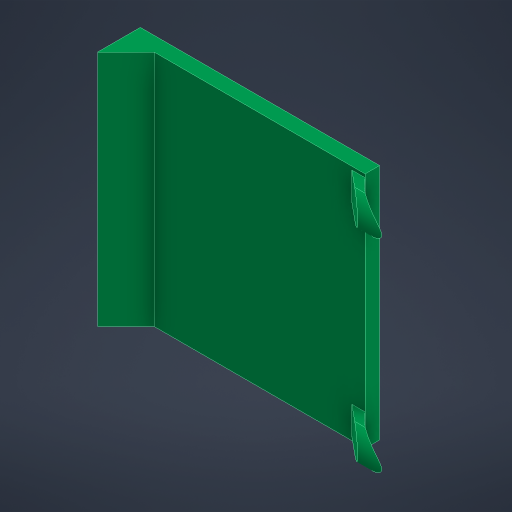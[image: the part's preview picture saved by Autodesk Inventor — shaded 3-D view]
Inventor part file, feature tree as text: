
AUTODESK INVENTOR PART (.ipt)
format: ipt  version: 2023.4 (Build 274418000, 418)  size: 428,032 bytes
history: native  units: mm
features: projected_geometry x15, extrude x8, reference x7, other x4, sketch x2, plane x2, fillet x1, mirror x1, chamfer x1
ambient origin geometry x8: Origin, YZ Plane, XZ Plane, XY Plane, X Axis, Y Axis, Z Axis, Center Point
bodies: Solid1 (feature_tree)
feature tree (41):
  extrude  "Extrusion1"  Depth=4.0mm
  sketch  "Sketch2"  dims[d2=4.0mm d3=4.0mm d4=4.0mm d5=2.0mm d6=2.0mm d7=2.0mm d8=2.0mm d9=3.0mm d10=1.9mm d11=45.0deg d12=33.75mm d13=0.0mm d17=1.5mm d18=0.15mm d19=4.0mm d20=0.0mm d21=2.0mm d22=1.0mm d23=2.5mm d24=0.075mm d28=45.0deg d31=5.0mm d32=0.0mm d37=180.0deg d38=90.0deg d39=67.5deg d40=50.0mm d41=0.0mm d42=18.4mm d43=7.5mm d44=30.0mm d45=10.0mm d46=0.0mm d49=33.75mm d50=0.0mm d52=40.0mm d53=0.0mm d54=0.025mm d55=0.15mm d56=0.15mm d57=10.0mm d58=0.0mm d59=1.35mm d60=2.0mm d61=45.0deg]
  plane  "Work Plane2"
  extrude  "Extrusion2"  Depth=10.0mm
  fillet  "Fillet1"  Radius=4.0mm
  extrude  "Extrusion3"  Depth=10.0mm
  mirror  "Mirror1"
  extrude  "Extrusion5"  Depth=10.0mm
  extrude  "Extrusion6"  Depth=10.0mm
  extrude  "Extrusion7"  Depth=10.0mm
  extrude  "Extrusion8"  Depth=10.0mm
  extrude  "Extrusion9"  Depth=10.0mm
  chamfer  "Chamfer2"  Angle=45.0deg  [1 undecoded]
  sketch  "Sketch1"  dims[d0=0.15mm d1=4.0mm]
  reference  "Reference1"
  reference  "Reference2"
  reference  "Reference3"
  projected_geometry  "Projected Loop1"
  reference  "Reference4"
  reference  "Reference5"
  reference  "Reference6"
  reference  "Reference7"
  other  "Work Point1"
  plane  "Work Plane1"
  projected_geometry  "Projected Loop4"
  projected_geometry  "Projected Loop5"
  projected_geometry  "Projected Loop6"
  projected_geometry  "Projected Loop7"
  projected_geometry  "Projected Loop8"
  projected_geometry  "Projected Loop9"
  projected_geometry  "Projected Loop14"
  projected_geometry  "Projected Loop15"
  projected_geometry  "Projected Loop16"
  projected_geometry  "Projected Loop17"
  projected_geometry  "Projected Loop18"
  projected_geometry  "Projected Loop19"
  projected_geometry  "Projected Loop20"
  projected_geometry  "Projected Loop21"
  other  "Cube 1x1 V5.iam"
  other  "Cube 1x1 Bottom V5:1"
  other  "Cube 1x1 Top V5:1"
note: 1 required parameter value undecoded (feature->parameter linkage not recoverable at this tier; creation-order binding heuristic only, values carry confidence <= 0.55)
